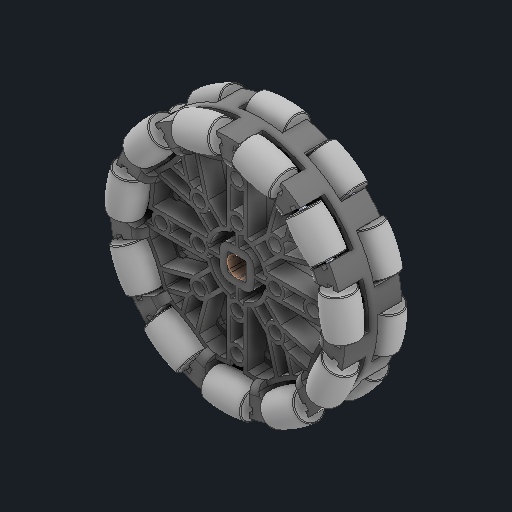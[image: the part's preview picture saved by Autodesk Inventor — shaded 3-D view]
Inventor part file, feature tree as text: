
AUTODESK INVENTOR PART (.ipt)
format: ipt  version: 2024 (Build 280153000, 153)  size: 3,350,016 bytes
history: native  units: in
note: dims shown in document units (in); Inventor stores cm internally (conversion verified against a paired STEP export)
features: other x49, sketch x1
ambient origin geometry x8: Origin, YZ Plane, XZ Plane, XY Plane, X Axis, Y Axis, Z Axis, Center Point
bodies: Solid1 (feature_tree), Solid2 (feature_tree), Solid3 (feature_tree), Solid4 (feature_tree), Solid5 (feature_tree), Solid6 (feature_tree), Solid7 (feature_tree), Solid8 (feature_tree), Solid9 (feature_tree), Solid10 (feature_tree), Solid11 (feature_tree), Solid12 (feature_tree), Solid13 (feature_tree), Solid14 (feature_tree), Solid15 (feature_tree), Solid16 (feature_tree), Solid17 (feature_tree), Solid18 (feature_tree), Solid19 (feature_tree), Solid20 (feature_tree), Solid21 (feature_tree), Solid22 (feature_tree), Solid23 (feature_tree), Solid24 (feature_tree), Solid25 (feature_tree), Solid26 (feature_tree), Solid27 (feature_tree), Solid28 (feature_tree), Solid29 (feature_tree), Solid30 (feature_tree), Solid31 (feature_tree), Solid32 (feature_tree), Solid33 (feature_tree), Solid34 (feature_tree), Solid35 (feature_tree), Solid36 (feature_tree), Solid37 (feature_tree), Solid38 (feature_tree), Solid39 (feature_tree), Solid40 (feature_tree), Solid41 (feature_tree), Solid42 (feature_tree), Solid43 (feature_tree), Solid44 (feature_tree), Solid45 (feature_tree)
feature tree (50):
  other  "3.25 Omni Antistatic.ipt"
  other  "Solid1::3.25 Omni Antistatic.ipt"
  other  "Solid2::3.25 Omni Antistatic.ipt"
  other  "Solid3::3.25 Omni Antistatic.ipt"
  other  "Solid4::3.25 Omni Antistatic.ipt"
  other  "Solid5::3.25 Omni Antistatic.ipt"
  other  "Solid6::3.25 Omni Antistatic.ipt"
  other  "Solid7::3.25 Omni Antistatic.ipt"
  other  "Solid8::3.25 Omni Antistatic.ipt"
  other  "Solid9::3.25 Omni Antistatic.ipt"
  other  "Solid10::3.25 Omni Antistatic.ipt"
  other  "Solid11::3.25 Omni Antistatic.ipt"
  other  "Solid12::3.25 Omni Antistatic.ipt"
  other  "Solid13::3.25 Omni Antistatic.ipt"
  other  "Solid14::3.25 Omni Antistatic.ipt"
  other  "Solid15::3.25 Omni Antistatic.ipt"
  other  "Solid16::3.25 Omni Antistatic.ipt"
  other  "Solid17::3.25 Omni Antistatic.ipt"
  other  "Solid18::3.25 Omni Antistatic.ipt"
  other  "Solid19::3.25 Omni Antistatic.ipt"
  other  "Solid20::3.25 Omni Antistatic.ipt"
  other  "Solid21::3.25 Omni Antistatic.ipt"
  other  "Solid22::3.25 Omni Antistatic.ipt"
  other  "Solid23::3.25 Omni Antistatic.ipt"
  other  "Solid24::3.25 Omni Antistatic.ipt"
  other  "Solid25::3.25 Omni Antistatic.ipt"
  other  "Solid26::3.25 Omni Antistatic.ipt"
  other  "Solid27::3.25 Omni Antistatic.ipt"
  other  "Solid28::3.25 Omni Antistatic.ipt"
  other  "Solid29::3.25 Omni Antistatic.ipt"
  other  "Solid30::3.25 Omni Antistatic.ipt"
  other  "Solid31::3.25 Omni Antistatic.ipt"
  other  "Solid32::3.25 Omni Antistatic.ipt"
  other  "Solid33::3.25 Omni Antistatic.ipt"
  other  "Solid34::3.25 Omni Antistatic.ipt"
  other  "Solid35::3.25 Omni Antistatic.ipt"
  other  "Solid36::3.25 Omni Antistatic.ipt"
  other  "Solid37::3.25 Omni Antistatic.ipt"
  other  "Solid38::3.25 Omni Antistatic.ipt"
  other  "Solid39::3.25 Omni Antistatic.ipt"
  other  "Solid40::3.25 Omni Antistatic.ipt"
  other  "Solid41::3.25 Omni Antistatic.ipt"
  other  "Solid42::3.25 Omni Antistatic.ipt"
  other  "Solid43::3.25 Omni Antistatic.ipt"
  other  "Solid44::3.25 Omni Antistatic.ipt"
  other  "Solid45::3.25 Omni Antistatic.ipt"
  other  "TaggingFeature1"
  sketch  "Sketch1"  dims[d0=0.3937in]
  other  "Srf1"
  other  "Srf1::Derived"
